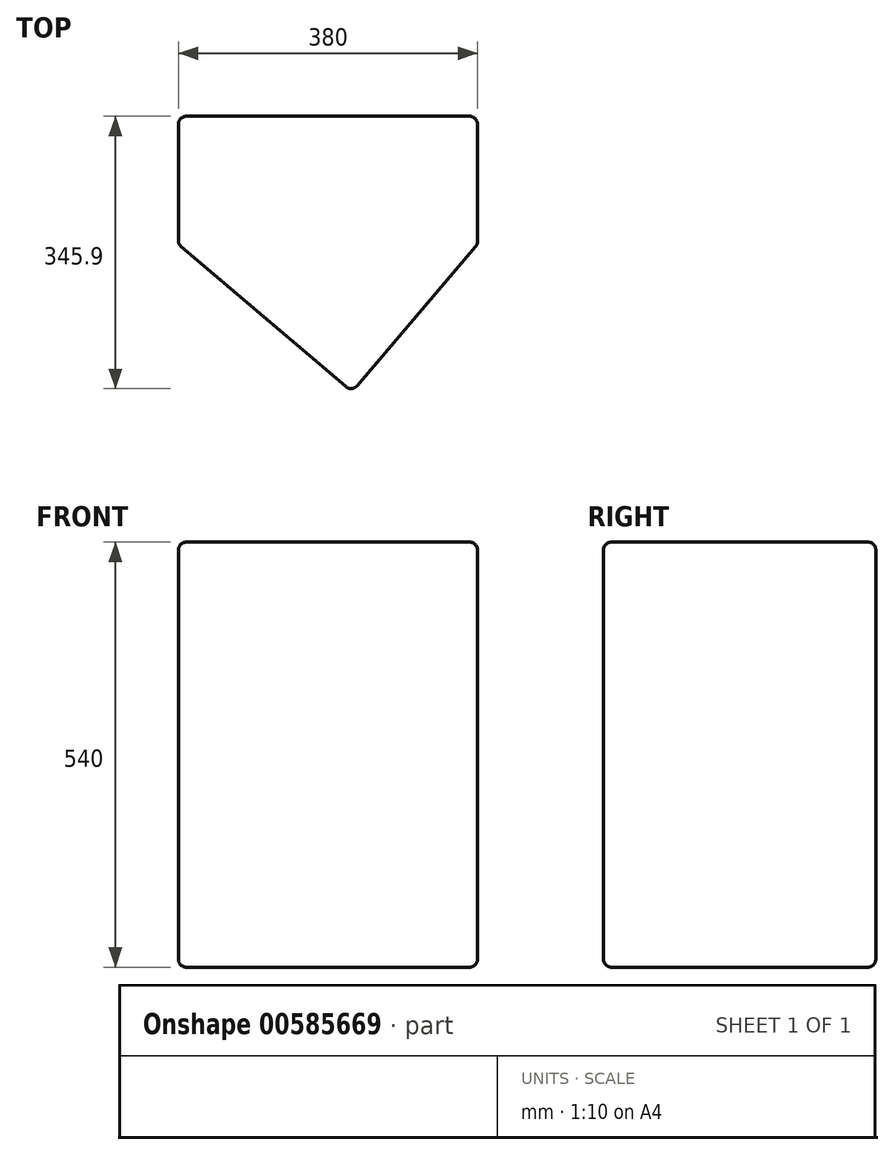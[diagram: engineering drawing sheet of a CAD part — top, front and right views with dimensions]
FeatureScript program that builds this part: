
annotation { "Feature Type Name" : "Feature", "Feature Type Description" : "" }
export const myFeature = defineFeature(function(context is Context, id is Id, definition is map)
    precondition{}
    {
        {
            var Q0;
            Q0=qCreatedBy(makeId("Top.planeOp"),FACE);
            var sketch = newSketch(context, id + "F0", { "sketchPlane" : qUnion([Q0])});
            skLineSegment(sketch, "E0", {"start": v(-220.36, 0) * mm, "end": v(159.64, 0) * mm});
            skLineSegment(sketch, "E1", {"start": v(159.64, 0) * mm, "end": v(159.64, -162.44) * mm});
            skLineSegment(sketch, "E2", {"start": v(159.64, -162.44) * mm, "end": v(0, -350) * mm});
            skLineSegment(sketch, "E3", {"start": v(0, -350) * mm, "end": v(-220.36, -162.44) * mm});
            skLineSegment(sketch, "E4", {"start": v(-220.36, -162.44) * mm, "end": v(-220.36, 0) * mm});
            skSolve(sketch);
        }
        {
            var Q0;
            Q0=makeQuery(id+"F0.imprint","IMPRINT",FACE,{"disambiguationData":[TD([[makeQuery(id+"F0.imprint","IMPRINT",EDGE,{"derivedFrom":sQuery(id+"F0.wireOp",EDGE,"E0")}),-1.0]])]});
            extrude(context, id + "F1", {"entities" : qUnion([Q0]), "endBound" : BoundingType.SYMMETRIC, "depth" : 540 * mm, "offsetDistance" : 25 * mm});
        }
        {
            var Q0;
            Q0=makeQuery(id+"F1.opExtrude","SWEPT_FACE",FACE,{"disambiguationData":[OSD([sQuery(id+"F0.wireOp",EDGE,"E4")])]});
            var Q1;
            Q1=makeQuery(id+"F1.opExtrude","SWEPT_FACE",FACE,{"disambiguationData":[OSD([sQuery(id+"F0.wireOp",EDGE,"E3")])]});
            var Q2;
            Q2=makeQuery(id+"F1.opExtrude","SWEPT_FACE",FACE,{"disambiguationData":[OSD([sQuery(id+"F0.wireOp",EDGE,"E2")])]});
            var Q3;
            Q3=makeQuery(id+"F1.opExtrude","SWEPT_FACE",FACE,{"disambiguationData":[OSD([sQuery(id+"F0.wireOp",EDGE,"E1")])]});
            var Q4;
            Q4=makeQuery(id+"F1.opExtrude","SWEPT_FACE",FACE,{"disambiguationData":[OSD([sQuery(id+"F0.wireOp",EDGE,"E0")])]});
            fillet(context, id + "F2", {"entities" : qUnion([Q0, Q1, Q2, Q3, Q4]), "radius" : 10 * mm, "tangentPropagation" : true, "allowEdgeOverflow" : false});
        }
    });
